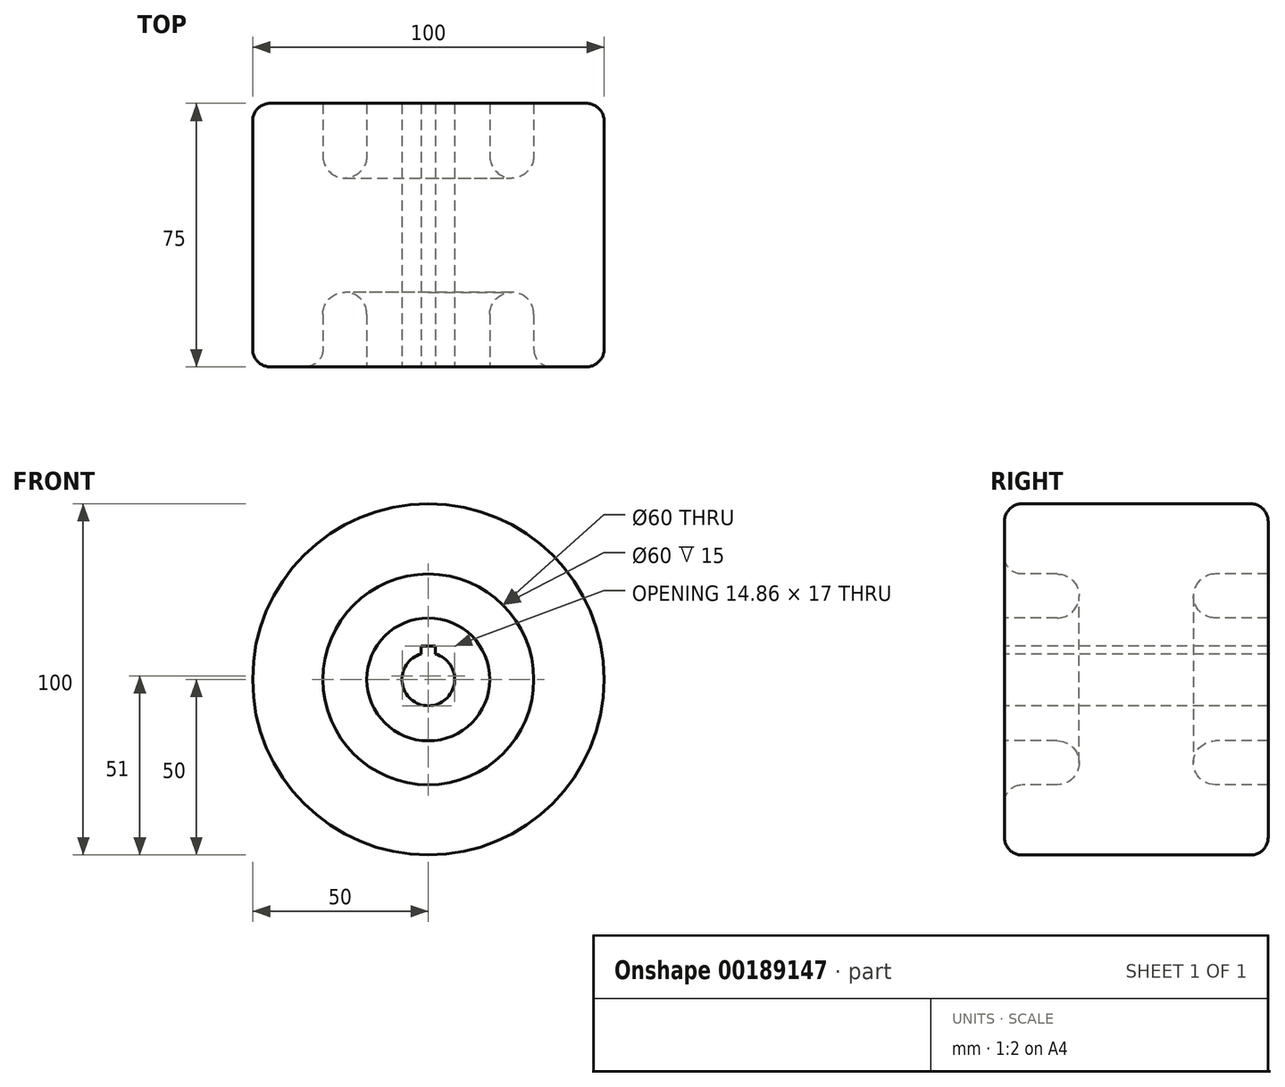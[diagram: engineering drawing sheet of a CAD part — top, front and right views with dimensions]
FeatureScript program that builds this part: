
annotation { "Feature Type Name" : "Feature", "Feature Type Description" : "" }
export const myFeature = defineFeature(function(context is Context, id is Id, definition is map)
    precondition{}
    {
        {
            var Q0;
            Q0=qCreatedBy(makeId("Right.planeOp"),FACE);
            var sketch = newSketch(context, id + "F0", { "sketchPlane" : qUnion([Q0])});
            skLineSegment(sketch, "E0", {"start": v(0, 0) * mm, "end": v(0, 7.5) * mm, "construction": true});
            skLineSegment(sketch, "E1", {"start": v(0, 7.5) * mm, "end": v(37.5, 7.5) * mm, "construction": true});
            skLineSegment(sketch, "E2", {"start": v(0, 0) * mm, "end": v(0, 50) * mm, "construction": true});
            skPoint(sketch, "E2.endSnap0", {"position": v(0, 3.75) * mm});
            skLineSegment(sketch, "E3", {"start": v(37.5, 7.5) * mm, "end": v(0, 7.5) * mm});
            skLineSegment(sketch, "E4", {"start": v(0, 50) * mm, "end": v(37.5, 50) * mm});
            skLineSegment(sketch, "E5", {"start": v(37.5, 7.5) * mm, "end": v(37.5, 17.5) * mm, "construction": true});
            skLineSegment(sketch, "E6", {"start": v(37.5, 17.5) * mm, "end": v(22.5, 17.5) * mm, "construction": true});
            skLineSegment(sketch, "E7", {"start": v(37.5, 50) * mm, "end": v(37.5, 30) * mm, "construction": true});
            skLineSegment(sketch, "E8", {"start": v(37.5, 30) * mm, "end": v(22.5, 30) * mm, "construction": true});
            skLineSegment(sketch, "E9", {"start": v(37.5, 30) * mm, "end": v(37.5, 50) * mm});
            skLineSegment(sketch, "E10", {"start": v(37.5, 30) * mm, "end": v(22.5, 30) * mm});
            skLineSegment(sketch, "E11", {"start": v(37.5, 17.5) * mm, "end": v(22.5, 17.5) * mm});
            skLineSegment(sketch, "E12", {"start": v(37.5, 17.5) * mm, "end": v(37.5, 7.5) * mm});
            skLineSegment(sketch, "E13", {"start": v(22.5, 17.5) * mm, "end": v(37.5, 17.5) * mm});
            skArc(sketch, "E14", {"start": v(22.5, 30) * mm, "mid": v(16.25, 23.75) * mm, "end": v(22.5, 17.5) * mm});
            skLineSegment(sketch, "E15.MirrorCS", {"start": v(-37.5, 17.5) * mm, "end": v(-22.5, 17.5) * mm});
            skLineSegment(sketch, "E16.MirrorCS", {"start": v(-37.5, 30) * mm, "end": v(-22.5, 30) * mm});
            skLineSegment(sketch, "E17.MirrorCS", {"start": v(-37.5, 17.5) * mm, "end": v(-37.5, 7.5) * mm});
            skLineSegment(sketch, "E18.MirrorCS", {"start": v(-22.5, 17.5) * mm, "end": v(-37.5, 17.5) * mm});
            skLineSegment(sketch, "E19.MirrorCS", {"start": v(-37.5, 30) * mm, "end": v(-37.5, 50) * mm});
            skLineSegment(sketch, "E20.MirrorCS", {"start": v(-37.5, 50) * mm, "end": v(-37.5, 30) * mm, "construction": true});
            skLineSegment(sketch, "E21.MirrorCS", {"start": v(-37.5, 7.5) * mm, "end": v(-37.5, 17.5) * mm, "construction": true});
            skArc(sketch, "E22.MirrorCS", {"start": v(-22.5, 30) * mm, "mid": v(-16.25, 23.75) * mm, "end": v(-22.5, 17.5) * mm});
            skLineSegment(sketch, "E23.MirrorCS", {"start": v(-37.5, 17.5) * mm, "end": v(-22.5, 17.5) * mm, "construction": true});
            skLineSegment(sketch, "E24.MirrorCS", {"start": v(-37.5, 30) * mm, "end": v(-22.5, 30) * mm, "construction": true});
            skLineSegment(sketch, "E25.MirrorCS", {"start": v(0, 50) * mm, "end": v(-37.5, 50) * mm});
            skLineSegment(sketch, "E26", {"start": v(-37.5, 7.5) * mm, "end": v(0, 7.5) * mm});
            skLineSegment(sketch, "E27", {"start": v(-37.5, 0) * mm, "end": v(37.5, 0) * mm, "construction": true});
            skSolve(sketch);
        }
        {
            var Q0;
            Q0=makeQuery(id+"F0.imprint","IMPRINT",FACE,{"disambiguationData":[TD([[makeQuery(id+"F0.imprint","IMPRINT",EDGE,{"derivedFrom":sQuery(id+"F0.wireOp",EDGE,"E3")}),-1.0]])]});
            var Q1;
            Q1=sQuery(id+"F0.wireOp",EDGE,"E27");
            revolve(context, id + "F1", {"entities" : qUnion([Q0]), "axis" : qUnion([Q1]), "revolveType" : RevolveType.FULL});
        }
        {
            var Q0;
            Q0=makeQuery(id+"F1.opRevolve","SWEPT_FACE",FACE,{"disambiguationData":[OSD([sQuery(id+"F0.wireOp",EDGE,"E17.MirrorCS")])]});
            var sketch = newSketch(context, id + "F2", { "sketchPlane" : qUnion([Q0])});
            skLineSegment(sketch, "E28", {"start": v(0, 7.5) * mm, "end": v(0, 9.5) * mm, "construction": true});
            skLineSegment(sketch, "E29", {"start": v(0, 9.5) * mm, "end": v(2, 9.5) * mm, "construction": true});
            skLineSegment(sketch, "E30", {"start": v(2, 9.5) * mm, "end": v(2, 7.23) * mm, "construction": true});
            skLineSegment(sketch, "E31", {"start": v(0, 9.5) * mm, "end": v(-2, 9.5) * mm, "construction": true});
            skLineSegment(sketch, "E32", {"start": v(-2, 9.5) * mm, "end": v(-2, 7.23) * mm, "construction": true});
            skLineSegment(sketch, "E33", {"start": v(-2, 7.23) * mm, "end": v(-2, 9.5) * mm});
            skLineSegment(sketch, "E34", {"start": v(2, 9.5) * mm, "end": v(2, 7.23) * mm});
            skLineSegment(sketch, "E35", {"start": v(2, 9.5) * mm, "end": v(-2, 9.5) * mm});
            skSolve(sketch);
        }
        {
            var Q0;
            Q0 = qSketchRegion(id + "F2", true);
            var Q1;
            {var subQ0=sQuery(id+"F2.wireOp",EDGE,"E33");Q1=makeQuery(id+"F2.imprint","IMPRINT",FACE,{"disambiguationData":[TD([[makeQuery(id+"F2.imprint","IMPRINT",EDGE,{"derivedFrom":subQ0}),-1.0]])]});}
            extrude(context, id + "F3", {"entities" : qUnion([Q0, Q1]), "operationType" : NewBodyOperationType.REMOVE, "endBound" : BoundingType.THROUGH_ALL, "oppositeDirection" : true, "depth" : 25 * mm});
        }
        {
            var Q0;
            Q0=makeQuery(id+"F1.opRevolve","SWEPT_EDGE",EDGE,{"disambiguationData":[OSD([sQuery(id+"F0.wireOp",EDGE,"E16.MirrorCS"),sQuery(id+"F0.wireOp",EDGE,"E19.MirrorCS")])]});
            fillet(context, id + "F4", {"entities" : qUnion([Q0]), "radius" : 5 * mm, "tangentPropagation" : true, "allowEdgeOverflow" : false});
        }
        {
            var Q0;
            Q0=makeQuery(id+"F1.opRevolve","SWEPT_EDGE",EDGE,{"disambiguationData":[OSD([sQuery(id+"F0.wireOp",EDGE,"E19.MirrorCS"),sQuery(id+"F0.wireOp",EDGE,"E25.MirrorCS")])]});
            var Q1;
            Q1=makeQuery(id+"F1.opRevolve","SWEPT_EDGE",EDGE,{"disambiguationData":[OSD([sQuery(id+"F0.wireOp",EDGE,"E4"),sQuery(id+"F0.wireOp",EDGE,"E9")])]});
            fillet(context, id + "F5", {"entities" : qUnion([Q0, Q1]), "radius" : 5 * mm, "tangentPropagation" : true, "allowEdgeOverflow" : false});
        }
    });
